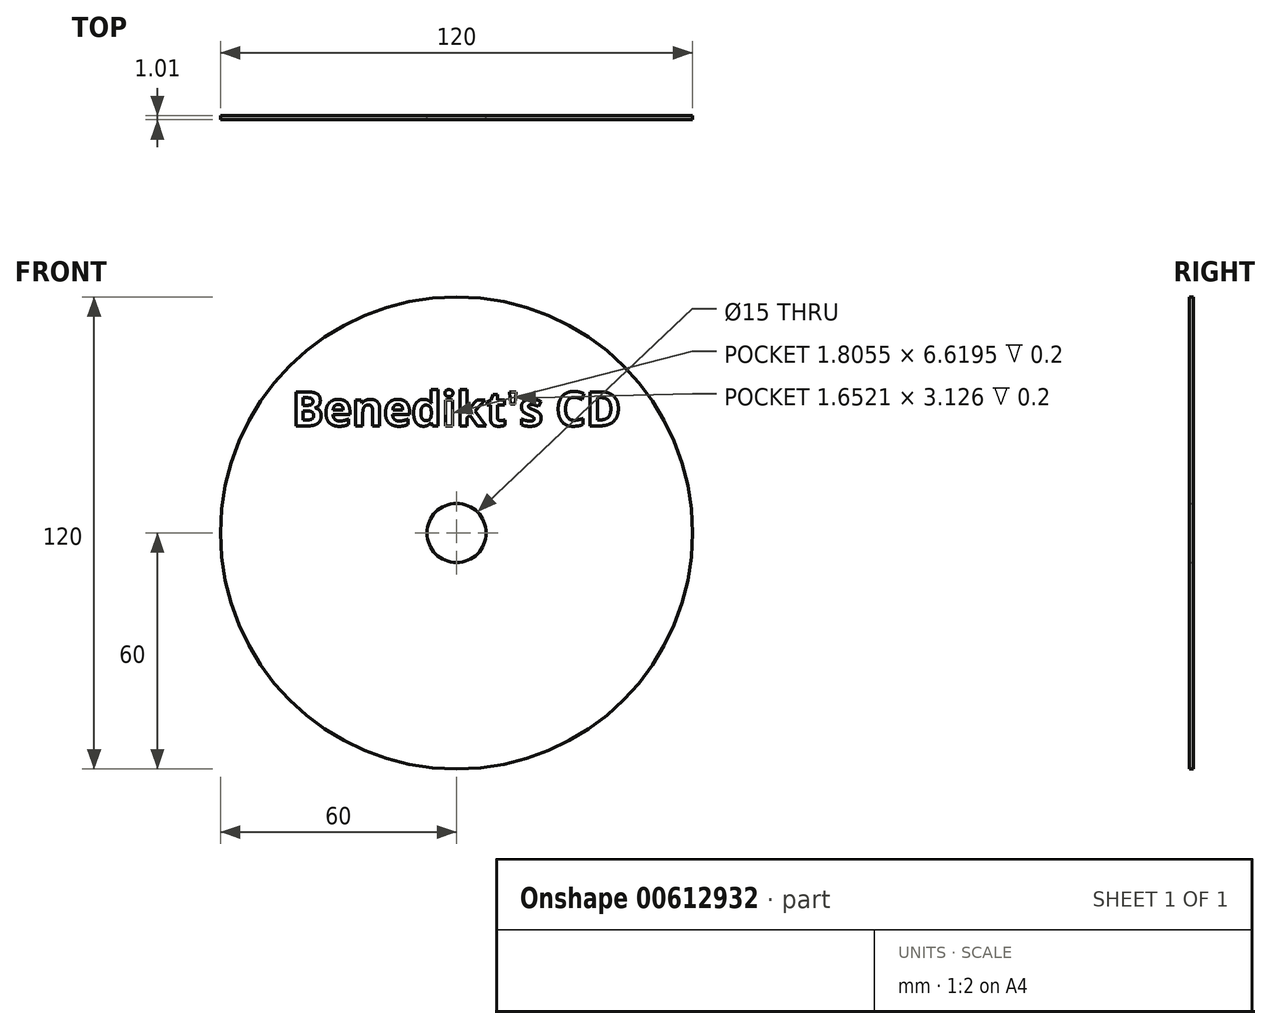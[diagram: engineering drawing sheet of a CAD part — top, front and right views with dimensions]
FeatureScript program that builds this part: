
annotation { "Feature Type Name" : "Feature", "Feature Type Description" : "" }
export const myFeature = defineFeature(function(context is Context, id is Id, definition is map)
    precondition{}
    {
        {
            var Q0;
            Q0=qCreatedBy(makeId("Front.planeOp"),FACE);
            var sketch = newSketch(context, id + "F0", { "sketchPlane" : qUnion([Q0])});
            skCircle(sketch, "E0", {"center": v(0, 0) * mm, "radius": 60 * mm});
            skCircle(sketch, "E1", {"center": v(0, 0) * mm, "radius": 7.5 * mm});
            skSolve(sketch);
        }
        {
            var Q0;
            Q0=makeQuery(id+"F0.imprint","IMPRINT",FACE,{"disambiguationData":[TD([[makeQuery(id+"F0.imprint","IMPRINT",EDGE,{"derivedFrom":sQuery(id+"F0.wireOp",EDGE,"E0")}),1.0]])]});
            extrude(context, id + "F1", {"entities" : qUnion([Q0]), "depth" : 1.01 * mm, "offsetDistance" : 25 * mm});
        }
        {
            var Q0;
            Q0=makeQuery(id+"F1.opExtrude","CAP_FACE",FACE,{"disambiguationData":[OSD([sQuery(id+"F0.wireOp",EDGE,"E0"),sQuery(id+"F0.wireOp",EDGE,"E1")])],"isStart":false});
            var sketch = newSketch(context, id + "F2", { "sketchPlane" : qUnion([Q0])});
            skText(sketch, "E2", { "text": "Benedikt\'s CD", "fontName": "OpenSans-Bold.ttf"});
            const initialGuessF2  = {"E2": [-0.04189, 0.02722, 1, 0, 0.00873]};
            skSetInitialGuess(sketch, initialGuessF2);
            skSolve(sketch);
        }
        {
            var Q0;
            Q0 = qSketchRegion(id + "F2", true);
            extrude(context, id + "F3", {"entities" : qUnion([Q0]), "operationType" : NewBodyOperationType.REMOVE, "oppositeDirection" : true, "depth" : 0.2 * mm, "offsetDistance" : 25 * mm});
        }
    });
